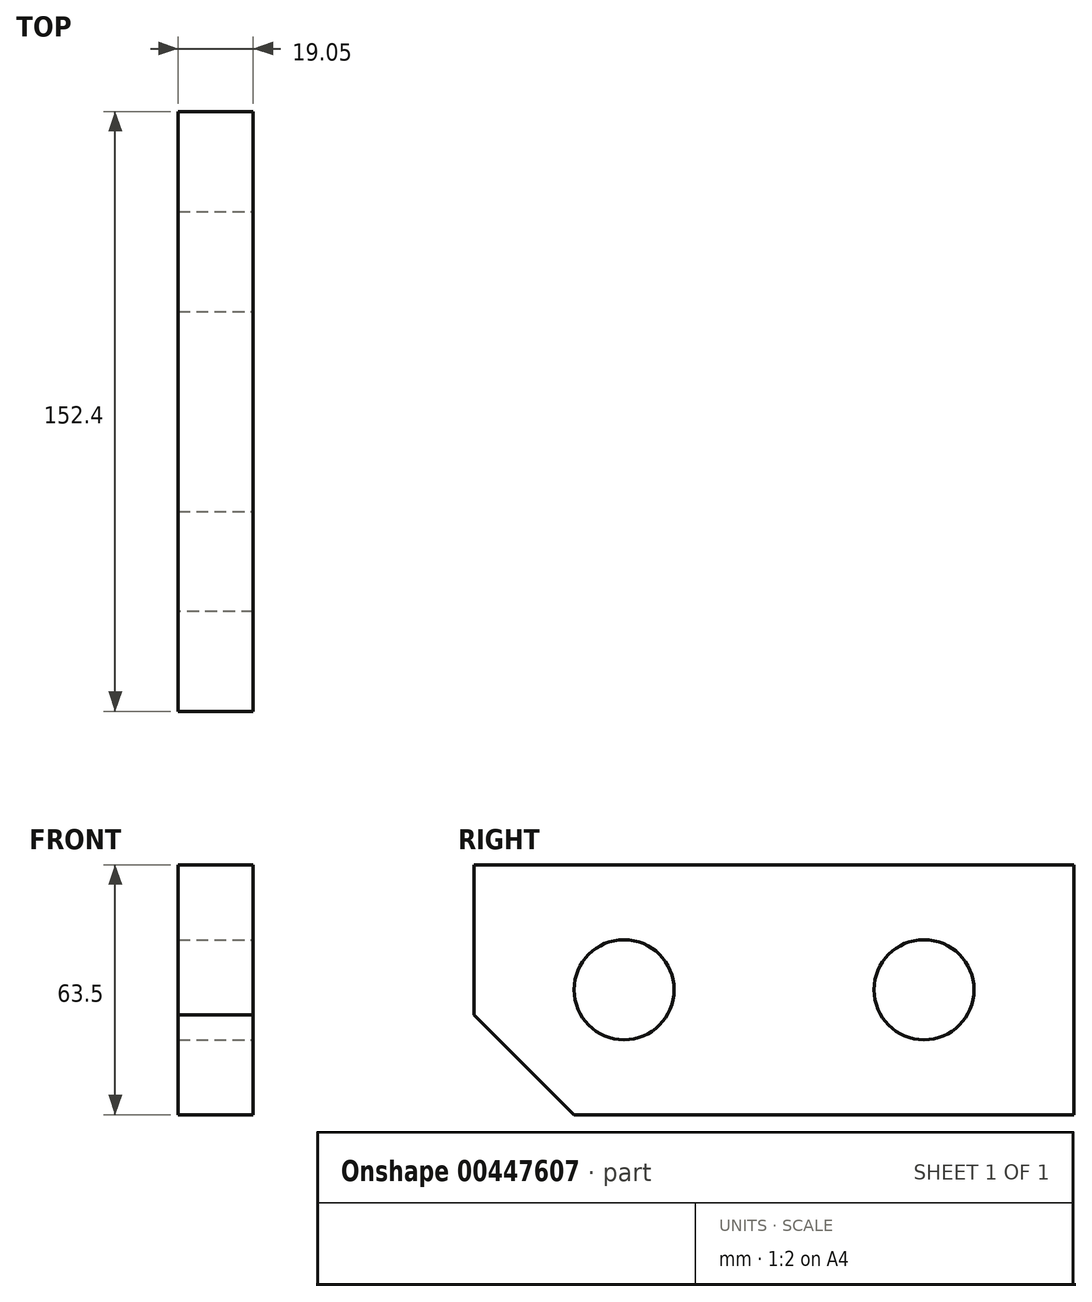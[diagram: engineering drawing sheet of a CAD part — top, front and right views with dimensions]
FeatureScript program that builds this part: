
annotation { "Feature Type Name" : "Feature", "Feature Type Description" : "" }
export const myFeature = defineFeature(function(context is Context, id is Id, definition is map)
    precondition{}
    {
        {
            var Q0;
            Q0=qCreatedBy(makeId("Front.planeOp"),FACE);
            var sketch = newSketch(context, id + "F0", { "sketchPlane" : qUnion([Q0])});
            skLineSegment(sketch, "E0.bottom", {"start": v(0, 0) * mm, "end": v(19.05, 0) * mm});
            skLineSegment(sketch, "E0.top", {"start": v(0, 63.5) * mm, "end": v(19.05, 63.5) * mm});
            skLineSegment(sketch, "E0.left", {"start": v(0, 0) * mm, "end": v(0, 63.5) * mm});
            skLineSegment(sketch, "E0.right", {"start": v(19.05, 0) * mm, "end": v(19.05, 63.5) * mm});
            skSolve(sketch);
        }
        {
            var Q0;
            Q0 = qSketchRegion(id + "F0", true);
            extrude(context, id + "F1", {"entities" : qUnion([Q0]), "depth" : 152.4 * mm, "offsetDistance" : 25.4 * mm});
        }
        {
            var Q0;
            Q0=makeQuery(id+"F1.opExtrude","CAP_EDGE",EDGE,{"disambiguationData":[OSD([sQuery(id+"F0.wireOp",EDGE,"E0.bottom")])],"isStart":false});
            chamfer(context, id + "F2", {"entities" : qUnion([Q0]), "width" : 25.4 * mm, "tangentPropagation" : true});
        }
        {
            var Q0;
            Q0=makeQuery(id+"F1.opExtrude","SWEPT_FACE",FACE,{"disambiguationData":[OSD([sQuery(id+"F0.wireOp",EDGE,"E0.right")])]});
            var sketch = newSketch(context, id + "F3", { "sketchPlane" : qUnion([Q0])});
            skCircle(sketch, "E1", {"center": v(-114.3, 31.75) * mm, "radius": 12.7 * mm});
            skCircle(sketch, "E2", {"center": v(-38.1, 31.75) * mm, "radius": 12.7 * mm});
            skSolve(sketch);
        }
        {
            var Q0;
            Q0 = qSketchRegion(id + "F3", true);
            extrude(context, id + "F4", {"entities" : qUnion([Q0]), "operationType" : NewBodyOperationType.REMOVE, "endBound" : BoundingType.THROUGH_ALL, "oppositeDirection" : true, "depth" : 25.4 * mm, "offsetDistance" : 25.4 * mm});
        }
    });
